# Revit family: DM_Штора_ПротивопожарнаяГармошкаЗамкнутая_Doormaster_E-60
name_source: partatom
category: Двери
units: mm (PartAtom-declared; Revit-internal decimal feet)

## family parameters
Всегда вертикально = Да
На основе рабочей плоскости = Нет
Общий = Нет
При загрузке вырезать с полостями = Нет
Точка расчета площади = Нет

## types (2) — shared parameters
ADSK_URL страницы изделия = https://www.doormaster.ru
ADSK_Версия Revit = 2019
ADSK_Версия семейства = 1
ADSK_Единица измерения = шт.
ADSK_Завод-изготовитель = ООО «СТЦ Дормастер»
ADSK_Классификация нагрузок = Прочее
ADSK_Код изделия = 20.52.10.190.14.2.02
ADSK_Количество = 1
ADSK_Количество фаз = 1
ADSK_Коэффициент мощности = 1
ADSK_Марка = DOORMASTER-FIREPROF-SG
ADSK_Напряжение = 0 В
ADSK_Обозначение = ГОСТ Р 53307-2009
ADSK_Полная мощность = 0 В·А
ADSK_Предел огнестойкости = E-60
BL_BIM library = https://bimlib.pro
DM_Высота короба = 220 мм
DM_Монтаж короба = к потолку
DM_Ширина короба = 250 мм
DM_Щит управления = Щит управления : ЩУ-480-2
URL = https://www.doormaster.ru
Высота нижнего короба = 150 мм
Изготовитель = ООО «СТЦ Дормастер»
Материал короба = DM_Сталь_Холоднокатанная_08ПС
Материал полотна = DM_Ткань_Кремнеземная_Со специальной пропиткой
Огнестойкость = E-60
Описание = Противодымная контурная штора "Гармошка" представляет собой ограждающую конструкцию, которая автоматически раскрывается при возгорании или задымлении, образуя надежную завесу. Щит управления ЩУ-480-2 поставляется в комплекте
Тип конструкций = Штора противодымная "Гармошка"
Толщина = 1 мм
Четный = Да
Ширина складки = 250 мм
zero-valued in all types: ч3

## per-type parameters (varying)
- H=3000 A1=4000 B1=2500 B2=3500 (угол левый=110 угол правый=110): ADSK_Наименование=Противопожарная противодымная контурная штора "Гармошка" замкнутая H=3000, L=16125, угол левый=110°, угол правый=110° (ЩУ-480-2 в комплекте); ADSK_Наименование краткое=Противодымная штора "Гармошка" замкнутая H=3000, L=16125 (ЩУ-480-2 в комплекте); ADSK_Размер_Высота=3000 мм; ADSK_Размер_Длина=16125 мм; ADSK_Размер_Ширина=6052 мм; N=7; a1=855 мм; a2=1197 мм; b1=2349 мм; b2=3289 мм; d1=5394 мм; n=14; Высота=3000 мм; Примерная высота=2630 мм; Примерная ширина=6052 мм; Сторона A1=4000 мм; Сторона A2=6125 мм; Сторона B1=2500 мм; Сторона B2=3500 мм; У1=25.82°; У2=84.18°; Угол левый=110.00°; Угол левый_Геометрия=110.00°; Угол правый=110.00°; Угол правый_Геометрия=110.00°; Ширина=6052 мм; ч1=7; ч2=7
- H=4000 A1=6000 B1=3000 B2=3000 (угол левый=90 угол правый=90): ADSK_Наименование=Противопожарная противодымная контурная штора "Гармошка" замкнутая H=4000, L=18000, угол левый=90°, угол правый=90° (ЩУ-480-2 в комплекте); ADSK_Наименование краткое=Противодымная штора "Гармошка" замкнутая H=4000, L=18000 (ЩУ-480-2 в комплекте); ADSK_Размер_Высота=4000 мм; ADSK_Размер_Длина=18000 мм; ADSK_Размер_Ширина=6000 мм; N=10; a1=0 мм; a2=0 мм; b1=3000 мм; b2=3000 мм; d1=6708 мм; n=20; Высота=4000 мм; Примерная высота=3630 мм; Примерная ширина=6000 мм; Сторона A1=6000 мм; Сторона A2=6000 мм; Сторона B1=3000 мм; Сторона B2=3000 мм; У1=26.57°; У2=63.43°; Угол левый=90.00°; Угол левый_Геометрия=90.00°; Угол правый=90.00°; Угол правый_Геометрия=90.00°; Ширина=6000 мм; ч1=10; ч2=10
